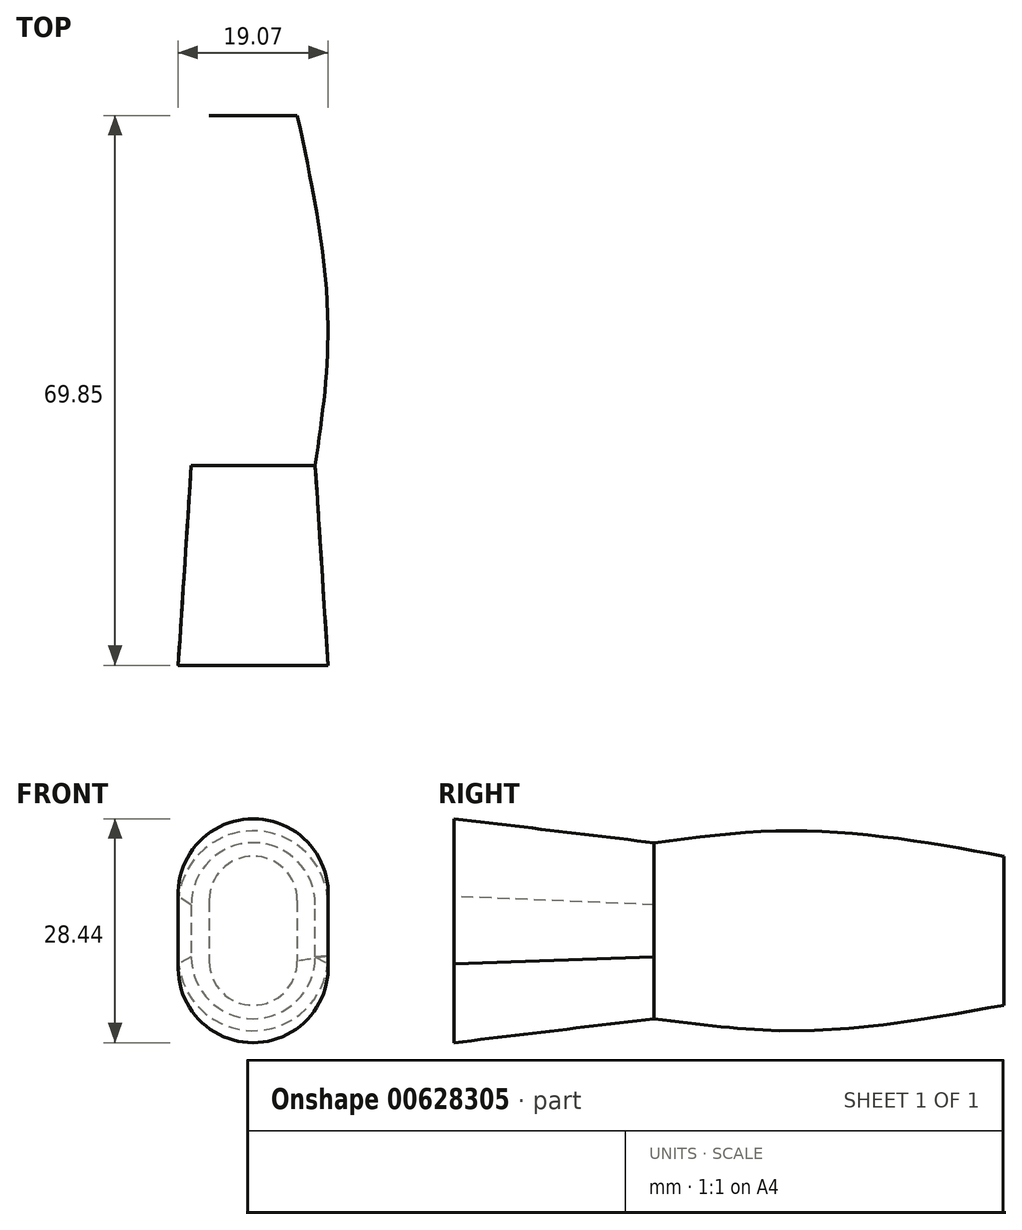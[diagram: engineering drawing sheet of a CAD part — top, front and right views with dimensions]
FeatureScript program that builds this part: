
annotation { "Feature Type Name" : "Feature", "Feature Type Description" : "" }
export const myFeature = defineFeature(function(context is Context, id is Id, definition is map)
    precondition{}
    {
        {
            var Q0;
            Q0=qCreatedBy(makeId("Front.planeOp"),FACE);
            var sketch = newSketch(context, id + "F0", { "sketchPlane" : qUnion([Q0])});
            skLineSegment(sketch, "E0", {"start": v(-5.59, 3.87) * mm, "end": v(-5.59, -3.87) * mm});
            skLineSegment(sketch, "E1", {"start": v(5.59, 3.87) * mm, "end": v(5.59, -3.87) * mm});
            skArc(sketch, "E2", {"start": v(5.59, 3.87) * mm, "mid": v(0, 9.46) * mm, "end": v(-5.59, 3.87) * mm});
            skArc(sketch, "E3", {"start": v(-5.59, -3.87) * mm, "mid": v(0, -9.46) * mm, "end": v(5.59, -3.87) * mm});
            skPoint(sketch, "E4.orphan", {"position": v(5.59, -3.87) * mm});
            skPoint(sketch, "E5.orphan", {"position": v(5.59, -9.46) * mm});
            skPoint(sketch, "E6.orphan", {"position": v(5.59, 9.46) * mm});
            skSolve(sketch);
        }
        {
            var Q0;
            Q0=qCreatedBy(makeId("Front.planeOp"),FACE);
            cPlane(context, id + "F1", {"entities" : qUnion([Q0]), "cplaneType" : CPlaneType.OFFSET, "offset" : 27.94 * mm, "width" : 152.4 * mm, "height" : 152.4 * mm});
        }
        {
            var Q0;
            Q0=qCreatedBy(id+"F1.planeOp",FACE);
            var sketch = newSketch(context, id + "F2", { "sketchPlane" : qUnion([Q0])});
            skLineSegment(sketch, "E7", {"start": v(-9.53, 3.18) * mm, "end": v(-9.53, -3.17) * mm});
            skLineSegment(sketch, "E8", {"start": v(9.52, -3.18) * mm, "end": v(9.52, 3.18) * mm});
            skArc(sketch, "E9", {"start": v(9.52, 3.18) * mm, "mid": v(0, 12.7) * mm, "end": v(-9.53, 3.18) * mm});
            skPoint(sketch, "E10.endSnap0", {"position": v(-9.53, -4.76) * mm});
            skArc(sketch, "E11", {"start": v(-9.53, -3.17) * mm, "mid": v(0, -12.7) * mm, "end": v(9.53, -3.18) * mm});
            skPoint(sketch, "E12.orphan", {"position": v(-9.53, -12.7) * mm});
            skSolve(sketch);
        }
        {
            var Q0;
            Q0=qCreatedBy(id+"F1.planeOp",FACE);
            cPlane(context, id + "F3", {"entities" : qUnion([Q0]), "cplaneType" : CPlaneType.OFFSET, "offset" : 16.5 * mm, "width" : 152.4 * mm, "height" : 152.4 * mm});
        }
        {
            var Q0;
            Q0=qCreatedBy(id+"F3.planeOp",FACE);
            var sketch = newSketch(context, id + "F4", { "sketchPlane" : qUnion([Q0])});
            skLineSegment(sketch, "E13", {"start": v(7.77, 4.57) * mm, "end": v(7.87, 4.57) * mm});
            skLineSegment(sketch, "E14", {"start": v(-7.87, 3.3) * mm, "end": v(-7.87, -3.3) * mm});
            skLineSegment(sketch, "E15", {"start": v(7.87, -3.3) * mm, "end": v(7.87, 3.3) * mm});
            skArc(sketch, "E16", {"start": v(7.87, 3.3) * mm, "mid": v(0, 11.18) * mm, "end": v(-7.87, 3.3) * mm});
            skArc(sketch, "E17", {"start": v(-7.87, -3.3) * mm, "mid": v(0, -11.18) * mm, "end": v(7.87, -3.3) * mm});
            skPoint(sketch, "E18.orphan", {"position": v(7.87, -11.18) * mm});
            skSolve(sketch);
        }
        {
            var Q0;
            Q0=qCreatedBy(id+"F3.planeOp",FACE);
            cPlane(context, id + "F5", {"entities" : qUnion([Q0]), "cplaneType" : CPlaneType.OFFSET, "offset" : 25.4 * mm, "width" : 152.4 * mm, "height" : 152.4 * mm});
        }
        {
            var Q0;
            Q0=qCreatedBy(id+"F5.planeOp",FACE);
            var sketch = newSketch(context, id + "F6", { "sketchPlane" : qUnion([Q0])});
            skLineSegment(sketch, "E19", {"start": v(9.5, 0) * mm, "end": v(9.53, 0) * mm});
            skArc(sketch, "E20", {"start": v(9.51, 4.33) * mm, "mid": v(0, 14.22) * mm, "end": v(-9.53, 4.34) * mm});
            skArc(sketch, "E21", {"start": v(-9.53, -4.2) * mm, "mid": v(-0.02, -14.22) * mm, "end": v(9.5, -4.21) * mm});
            skLineSegment(sketch, "E22", {"start": v(9.51, 4.33) * mm, "end": v(9.5, -4.21) * mm});
            skLineSegment(sketch, "E23", {"start": v(-9.53, 4.34) * mm, "end": v(-9.53, -4.2) * mm});
            skSolve(sketch);
        }
        {
            var Q0;
            {var subQ2=sQuery(id+"F4.wireOp",EDGE,"E14");Q0=makeQuery(id+"F4.imprint","IMPRINT",FACE,{"disambiguationData":[TD([[makeQuery(id+"F4.imprint","IMPRINT",EDGE,{"derivedFrom":subQ2}),1.0]])]});}
            var Q1;
            Q1=makeQuery(id+"F2.imprint","IMPRINT",FACE,{"disambiguationData":[TD([[makeQuery(id+"F2.imprint","IMPRINT",EDGE,{"derivedFrom":sQuery(id+"F2.wireOp",EDGE,"E7")}),1.0]])]});
            var Q2;
            Q2=makeQuery(id+"F0.imprint","IMPRINT",FACE,{"disambiguationData":[TD([[makeQuery(id+"F0.imprint","IMPRINT",EDGE,{"derivedFrom":sQuery(id+"F0.wireOp",EDGE,"E0")}),1.0]])]});
            loft(context, id + "F7", {"sheetProfilesArray" : [{ "sheetProfileEntities" : qUnion([Q0]) }, { "sheetProfileEntities" : qUnion([Q1]) }, { "sheetProfileEntities" : qUnion([Q2]) }]});
        }
        {
            var Q1;
            {var subQ2=sQuery(id+"F4.wireOp",EDGE,"E14");Q1=makeQuery(id+"F7.opLoft","CAP_FACE",FACE,{"disambiguationData":[OSD([makeQuery(id+"F4.imprint","IMPRINT",FACE,{"disambiguationData":[TD([[makeQuery(id+"F4.imprint","IMPRINT",EDGE,{"derivedFrom":subQ2}),1.0]])]})])],"isStart":true});}
            var Q2;
            {var subQ3=sQuery(id+"F6.wireOp",EDGE,"E20");Q2=makeQuery(id+"F6.imprint","IMPRINT",FACE,{"disambiguationData":[TD([[makeQuery(id+"F6.imprint","IMPRINT",EDGE,{"derivedFrom":subQ3}),1.0]])]});}
            loft(context, id + "F8", {"operationType" : NewBodyOperationType.ADD, "sheetProfilesArray" : [{ "sheetProfileEntities" : qUnion([Q1]) }, { "sheetProfileEntities" : qUnion([Q2]) }]});
        }
    });
